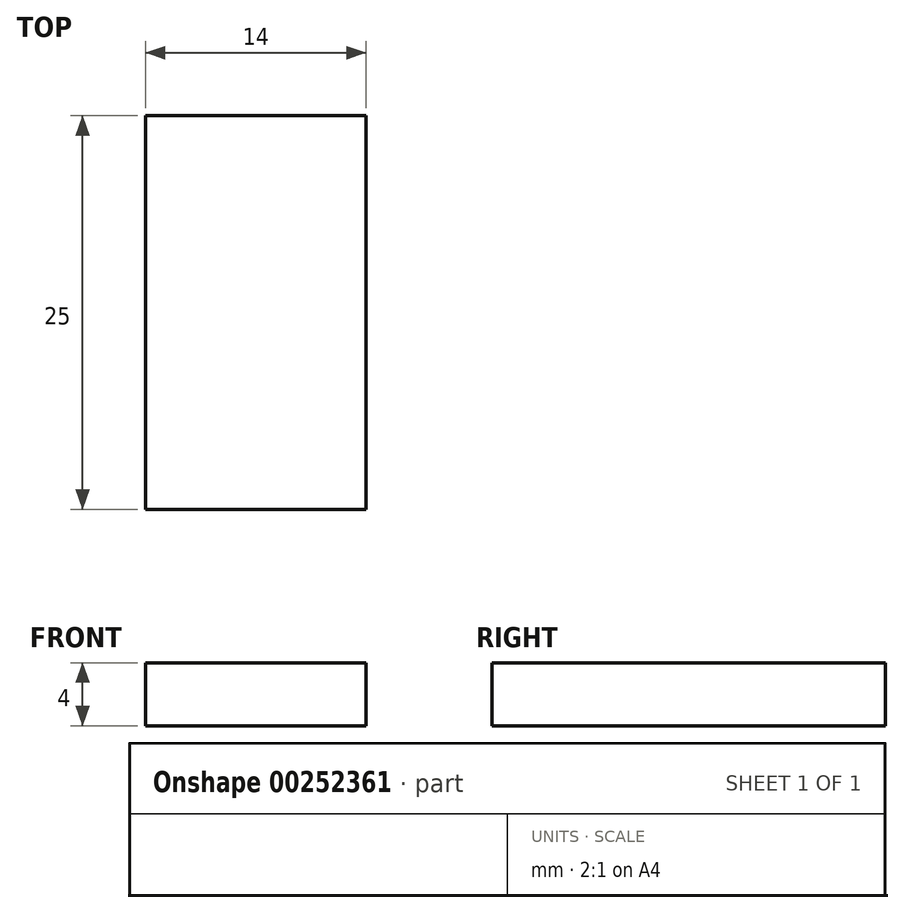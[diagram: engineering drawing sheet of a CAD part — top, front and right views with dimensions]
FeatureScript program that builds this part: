
annotation { "Feature Type Name" : "Feature", "Feature Type Description" : "" }
export const myFeature = defineFeature(function(context is Context, id is Id, definition is map)
    precondition{}
    {
        {
            var Q0;
            Q0=qCreatedBy(makeId("Front.planeOp"),FACE);
            var sketch = newSketch(context, id + "F0", { "sketchPlane" : qUnion([Q0])});
            skLineSegment(sketch, "E0.bottom", {"start": v(-7, 2) * mm, "end": v(7, 2) * mm});
            skLineSegment(sketch, "E0.top", {"start": v(-7, -2) * mm, "end": v(7, -2) * mm});
            skLineSegment(sketch, "E0.left", {"start": v(-7, 2) * mm, "end": v(-7, -2) * mm});
            skLineSegment(sketch, "E0.right", {"start": v(7, 2) * mm, "end": v(7, -2) * mm});
            skPoint(sketch, "E0.middle", {"position": v(0, 0) * mm});
            skSolve(sketch);
        }
        {
            var Q0;
            Q0=makeQuery(id+"F0.imprint","IMPRINT",FACE,{"disambiguationData":[TD([[makeQuery(id+"F0.imprint","IMPRINT",EDGE,{"derivedFrom":sQuery(id+"F0.wireOp",EDGE,"E0.bottom")}),-1.0]])]});
            extrude(context, id + "F1", {"entities" : qUnion([Q0]), "depth" : 25 * mm});
        }
    });
